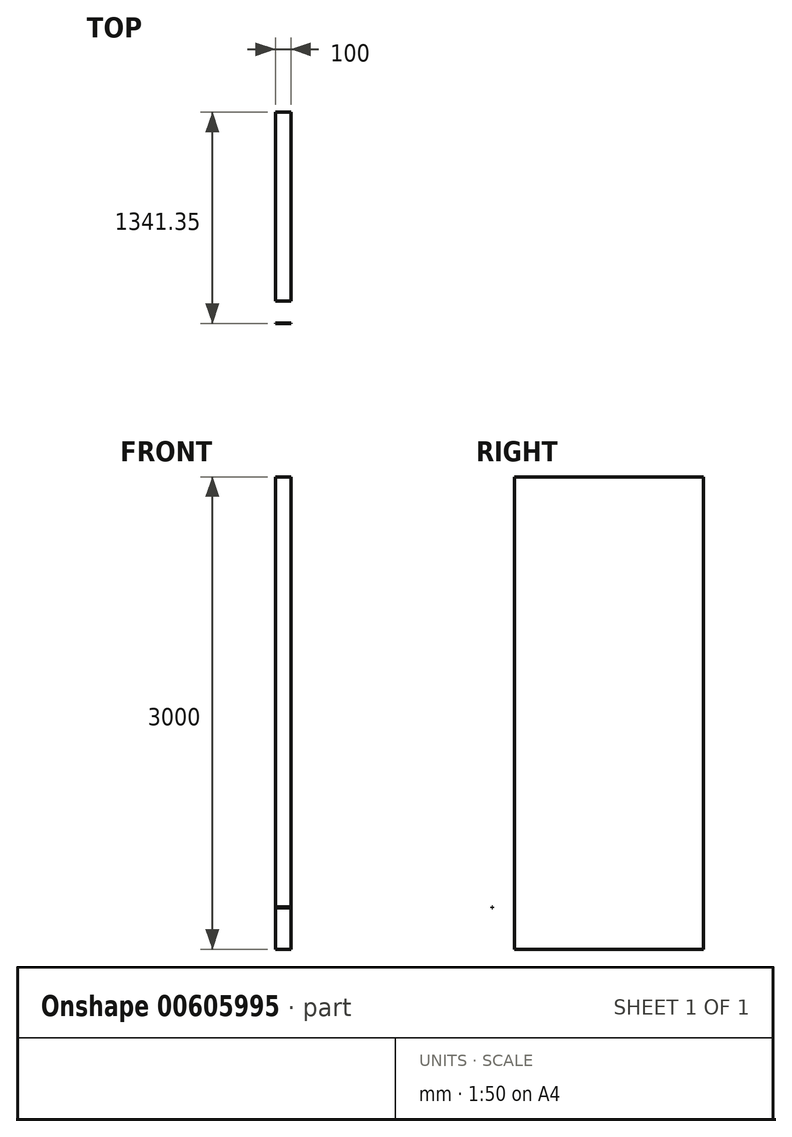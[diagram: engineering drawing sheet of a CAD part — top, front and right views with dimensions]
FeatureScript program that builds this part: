
annotation { "Feature Type Name" : "Feature", "Feature Type Description" : "" }
export const myFeature = defineFeature(function(context is Context, id is Id, definition is map)
    precondition{}
    {
        {
            var Q0;
            Q0=qCreatedBy(makeId("Right.planeOp"),FACE);
            var sketch = newSketch(context, id + "F0", { "sketchPlane" : qUnion([Q0])});
            skLineSegment(sketch, "E0.bottom", {"start": v(-206, 417.64) * mm, "end": v(-203.78, 417.64) * mm});
            skLineSegment(sketch, "E0.top", {"start": v(-206, 423.72) * mm, "end": v(-203.78, 423.72) * mm});
            skLineSegment(sketch, "E0.left", {"start": v(-206, 417.64) * mm, "end": v(-206, 423.72) * mm});
            skLineSegment(sketch, "E0.right", {"start": v(-203.78, 417.64) * mm, "end": v(-203.78, 423.72) * mm});
            skLineSegment(sketch, "E1.bottom", {"start": v(-64.64, 3154.2) * mm, "end": v(1135.36, 3154.2) * mm});
            skLineSegment(sketch, "E1.top", {"start": v(-64.64, 154.2) * mm, "end": v(1135.36, 154.2) * mm});
            skLineSegment(sketch, "E1.left", {"start": v(-64.64, 3154.2) * mm, "end": v(-64.64, 154.2) * mm});
            skLineSegment(sketch, "E1.right", {"start": v(1135.36, 3154.2) * mm, "end": v(1135.36, 154.2) * mm});
            skSolve(sketch);
        }
        {
            var Q0;
            Q0 = qSketchRegion(id + "F0", true);
            extrude(context, id + "F1", {"entities" : qUnion([Q0]), "depth" : 100 * mm, "offsetDistance" : 25 * mm});
        }
    });
